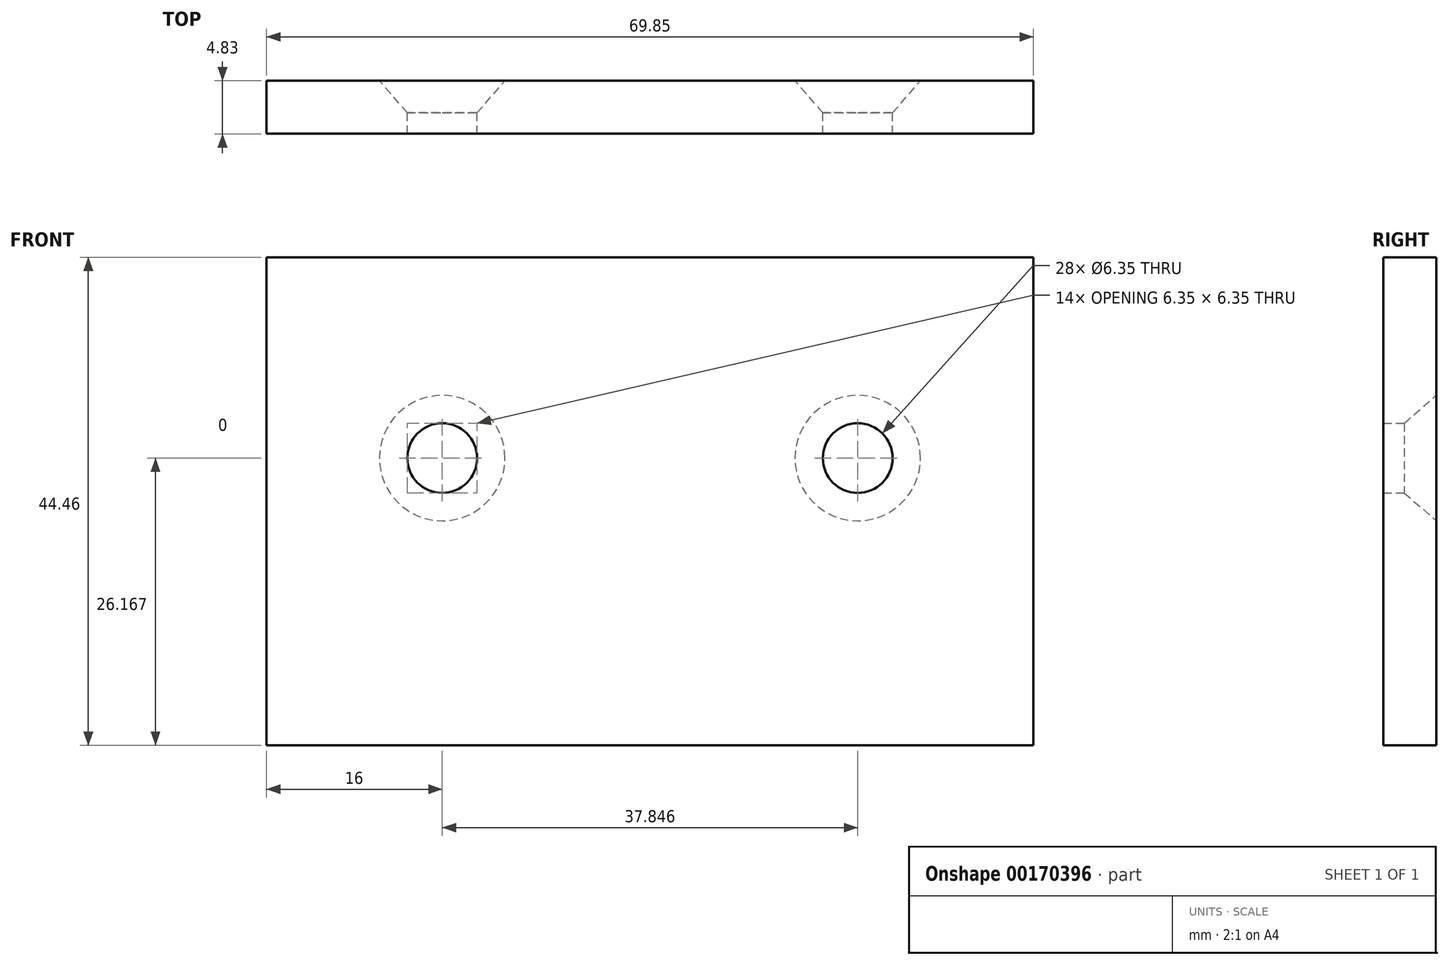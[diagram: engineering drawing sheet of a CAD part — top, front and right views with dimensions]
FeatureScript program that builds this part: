
annotation { "Feature Type Name" : "Feature", "Feature Type Description" : "" }
export const myFeature = defineFeature(function(context is Context, id is Id, definition is map)
    precondition{}
    {
        {
            var Q0;
            Q0=qCreatedBy(makeId("Front.planeOp"),FACE);
            var sketch = newSketch(context, id + "F0", { "sketchPlane" : qUnion([Q0])});
            skLineSegment(sketch, "E0.bottom", {"start": v(-35.05, 22.22) * mm, "end": v(34.8, 22.23) * mm});
            skLineSegment(sketch, "E0.top", {"start": v(-35.05, -22.22) * mm, "end": v(34.8, -22.22) * mm});
            skLineSegment(sketch, "E0.left", {"start": v(-35.05, 22.22) * mm, "end": v(-35.05, -22.22) * mm});
            skLineSegment(sketch, "E0.right", {"start": v(34.8, 22.23) * mm, "end": v(34.8, -22.22) * mm});
            skPoint(sketch, "E1", {"position": v(-19.05, 3.94) * mm});
            skPoint(sketch, "E2", {"position": v(18.8, 3.94) * mm});
            skSolve(sketch);
        }
        {
            var Q0;
            Q0=makeQuery(id+"F0.imprint","IMPRINT",FACE,{"disambiguationData":[TD([[makeQuery(id+"F0.imprint","IMPRINT",EDGE,{"derivedFrom":sQuery(id+"F0.wireOp",EDGE,"E0.bottom")}),-1.0]])]});
            extrude(context, id + "F1", {"entities" : qUnion([Q0]), "depth" : 4.83 * mm});
        }
        {
            var Q0;
            Q0=sQuery(id+"F0.wireOp",VERTEX,"E1");
            var Q1;
            Q1=sQuery(id+"F0.wireOp",VERTEX,"E2");
            var Q2;
            Q2=makeQuery(id+"F1.opExtrude","SWEPT_BODY",BODY,{"disambiguationData":[OSD([sQuery(id+"F0.wireOp",EDGE,"E0.bottom"),sQuery(id+"F0.wireOp",EDGE,"E0.top"),sQuery(id+"F0.wireOp",EDGE,"E0.left"),sQuery(id+"F0.wireOp",EDGE,"E0.right")])]});
            hole(context, id + "F2", {"style" : HoleStyle.C_SINK, "endStyle" : HoleEndStyle.THROUGH, "oppositeDirection" : true, "holeDiameter" : 6.35 * mm, "cSinkDiameter" : 11.43 * mm, "cSinkAngle" : 82 * degree, "locations" : qUnion([Q0, Q1]), "scope" : qUnion([Q2]), "isTappedThrough" : true});
        }
    });
